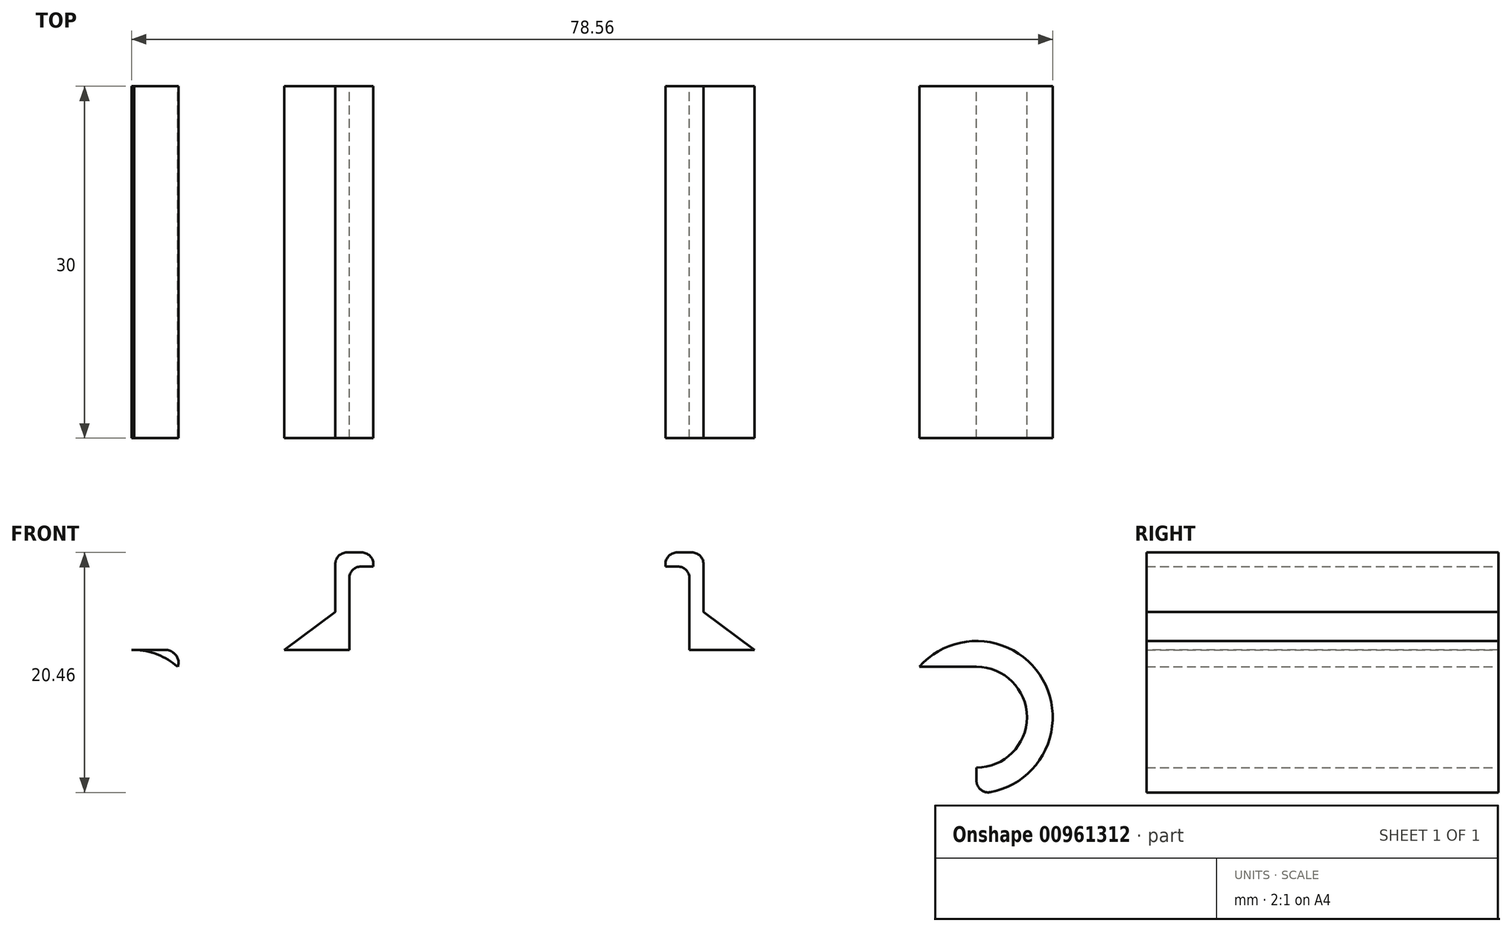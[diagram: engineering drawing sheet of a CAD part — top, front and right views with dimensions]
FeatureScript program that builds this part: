
annotation { "Feature Type Name" : "Feature", "Feature Type Description" : "" }
export const myFeature = defineFeature(function(context is Context, id is Id, definition is map)
    precondition{}
    {
        {
            var Q0;
            Q0=qCreatedBy(makeId("Front.planeOp"),FACE);
            var sketch = newSketch(context, id + "F0", { "sketchPlane" : qUnion([Q0])});
            skLineSegment(sketch, "E0", {"start": v(-37.32, 0) * mm, "end": v(43.18, 0) * mm});
            skCircle(sketch, "E1", {"center": v(-32.97, 0) * mm, "radius": 4.3 * mm});
            skCircle(sketch, "E2", {"center": v(38.98, 0) * mm, "radius": 4.3 * mm});
            skCircle(sketch, "E3", {"center": v(-32.97, 0) * mm, "radius": 5.75 * mm});
            skCircle(sketch, "E4", {"center": v(38.98, 0) * mm, "radius": 5.75 * mm});
            skLineSegment(sketch, "E5", {"start": v(-33.08, 5.75) * mm, "end": v(38.98, 5.75) * mm});
            skLineSegment(sketch, "E6.bottom", {"start": v(-14.5, 5.75) * mm, "end": v(-15.7, 5.75) * mm});
            skLineSegment(sketch, "E6.top", {"start": v(-14.5, 14.05) * mm, "end": v(-15.7, 14.05) * mm});
            skLineSegment(sketch, "E6.left", {"start": v(-14.5, 5.75) * mm, "end": v(-14.5, 14.05) * mm});
            skLineSegment(sketch, "E6.right", {"start": v(-15.7, 5.75) * mm, "end": v(-15.7, 14.05) * mm});
            skLineSegment(sketch, "E7.MirrorCS", {"start": v(14.5, 5.75) * mm, "end": v(14.5, 14.05) * mm});
            skLineSegment(sketch, "E8.MirrorCS", {"start": v(15.7, 5.75) * mm, "end": v(15.7, 14.05) * mm});
            skLineSegment(sketch, "E9.MirrorCS", {"start": v(14.5, 14.05) * mm, "end": v(15.7, 14.05) * mm});
            skLineSegment(sketch, "E10", {"start": v(-14.5, 9.9) * mm, "end": v(14.5, 9.9) * mm, "construction": true});
            skLineSegment(sketch, "E11.bottom", {"start": v(-14.5, 14.05) * mm, "end": v(-12.45, 14.05) * mm});
            skLineSegment(sketch, "E11.top", {"start": v(-14.5, 12.85) * mm, "end": v(-12.45, 12.85) * mm});
            skLineSegment(sketch, "E11.left", {"start": v(-14.5, 14.05) * mm, "end": v(-14.5, 12.85) * mm});
            skLineSegment(sketch, "E11.right", {"start": v(-12.45, 14.05) * mm, "end": v(-12.45, 12.85) * mm});
            skLineSegment(sketch, "E12", {"start": v(-15.7, 8.98) * mm, "end": v(-20.06, 5.75) * mm});
            skLineSegment(sketch, "E13.MirrorCS", {"start": v(14.5, 12.85) * mm, "end": v(12.45, 12.85) * mm});
            skLineSegment(sketch, "E14.MirrorCS", {"start": v(12.45, 14.05) * mm, "end": v(12.45, 12.85) * mm});
            skLineSegment(sketch, "E15.MirrorCS", {"start": v(14.5, 14.05) * mm, "end": v(12.45, 14.05) * mm});
            skLineSegment(sketch, "E16.MirrorCS", {"start": v(15.7, 8.98) * mm, "end": v(20.06, 5.75) * mm});
            skLineSegment(sketch, "E17", {"start": v(-604.46, 5.74) * mm, "end": v(-604.46, 4.54) * mm});
            skLineSegment(sketch, "E18", {"start": v(-33.1, 4.3) * mm, "end": v(38.98, 4.3) * mm});
            skCircle(sketch, "E19", {"center": v(-32.97, 0) * mm, "radius": 6.5 * mm});
            skCircle(sketch, "E20", {"center": v(38.98, 0) * mm, "radius": 6.5 * mm});
            skLineSegment(sketch, "E21", {"start": v(-33.1, 4.3) * mm, "end": v(-33.1, -12) * mm});
            skLineSegment(sketch, "E22", {"start": v(38.98, 4.3) * mm, "end": v(38.98, -15.81) * mm});
            skSolve(sketch);
        }
        {
            var Q0;
            {var subQ4=sQuery(id+"F0.wireOp",EDGE,"E4");var subQ6=makeQuery(id+"F0.imprint","INTERSECT",VERTEX,{"derivedFrom":[subQ4,sQuery(id+"F0.wireOp",EDGE,"E5")]});Q0=makeQuery(id+"F0.imprint","IMPRINT",FACE,{"disambiguationData":[TD([[makeQuery(id+"F0.imprint","IMPRINT",EDGE,{"disambiguationData":[TD([[subQ6,-1.0]])],"derivedFrom":subQ4}),1.0]])]});}
            var Q1;
            {var subQ4=sQuery(id+"F0.wireOp",EDGE,"E6.bottom");Q1=makeQuery(id+"F0.imprint","IMPRINT",FACE,{"disambiguationData":[TD([[makeQuery(id+"F0.imprint","IMPRINT",EDGE,{"derivedFrom":subQ4}),1.0]])]});}
            var Q2;
            {var subQ0=sQuery(id+"F0.wireOp",EDGE,"E5");var subQ1=sQuery(id+"F0.wireOp",EDGE,"E3");var subQ9=makeQuery(id+"F0.imprint","INTERSECT",VERTEX,{"disambiguationData":[OD(1.0)],"derivedFrom":[subQ1,subQ0]});Q2=makeQuery(id+"F0.imprint","IMPRINT",FACE,{"disambiguationData":[TD([[makeQuery(id+"F0.imprint","IMPRINT",EDGE,{"disambiguationData":[TD([[subQ9,1.0]])],"derivedFrom":subQ1}),1.0]])]});}
            var Q3;
            {var subQ3=sQuery(id+"F0.wireOp",EDGE,"E12");Q3=makeQuery(id+"F0.imprint","IMPRINT",FACE,{"disambiguationData":[TD([[makeQuery(id+"F0.imprint","IMPRINT",EDGE,{"derivedFrom":subQ3}),1.0]])]});}
            var Q4;
            {var subQ1=sQuery(id+"F0.wireOp",EDGE,"E6.bottom");Q4=makeQuery(id+"F0.imprint","IMPRINT",FACE,{"disambiguationData":[TD([[makeQuery(id+"F0.imprint","IMPRINT",EDGE,{"derivedFrom":subQ1}),-1.0]])]});}
            var Q5;
            {var subQ2=sQuery(id+"F0.wireOp",EDGE,"E13.MirrorCS");Q5=makeQuery(id+"F0.imprint","IMPRINT",FACE,{"disambiguationData":[TD([[makeQuery(id+"F0.imprint","IMPRINT",EDGE,{"derivedFrom":subQ2}),-1.0]])]});}
            var Q6;
            Q6=makeQuery(id+"F0.imprint","IMPRINT",FACE,{"disambiguationData":[TD([[makeQuery(id+"F0.imprint","IMPRINT",EDGE,{"derivedFrom":sQuery(id+"F0.wireOp",EDGE,"E11.bottom")}),-1.0]])]});
            var Q7;
            {var subQ0=sQuery(id+"F0.wireOp",EDGE,"E9.MirrorCS");Q7=makeQuery(id+"F0.imprint","IMPRINT",FACE,{"disambiguationData":[TD([[makeQuery(id+"F0.imprint","IMPRINT",EDGE,{"derivedFrom":subQ0}),-1.0]])]});}
            var Q8;
            {var subQ0=sQuery(id+"F0.wireOp",EDGE,"E16.MirrorCS");var subQ1=sQuery(id+"F0.wireOp",EDGE,"E5");var subQ2=makeQuery(id+"F0.imprint","INTERSECT",VERTEX,{"derivedFrom":[subQ1,subQ0]});Q8=makeQuery(id+"F0.imprint","IMPRINT",FACE,{"disambiguationData":[TD([[makeQuery(id+"F0.imprint","IMPRINT",EDGE,{"disambiguationData":[TD([[subQ2,1.0]])],"derivedFrom":subQ1}),1.0]])]});}
            var Q9;
            {var subQ3=sQuery(id+"F0.wireOp",EDGE,"E5");var subQ5=sQuery(id+"F0.wireOp",EDGE,"E3");var subQ8=makeQuery(id+"F0.imprint","INTERSECT",VERTEX,{"disambiguationData":[OD(0.0)],"derivedFrom":[subQ5,subQ3]});Q9=makeQuery(id+"F0.imprint","IMPRINT",FACE,{"disambiguationData":[TD([[makeQuery(id+"F0.imprint","IMPRINT",EDGE,{"disambiguationData":[TD([[subQ8,1.0]])],"derivedFrom":subQ5}),-1.0]])]});}
            var Q10;
            {var subQ0=sQuery(id+"F0.wireOp",EDGE,"E18");var subQ1=sQuery(id+"F0.wireOp",EDGE,"E3");var subQ2=makeQuery(id+"F0.imprint","INTERSECT",VERTEX,{"derivedFrom":[subQ1,subQ0]});Q10=makeQuery(id+"F0.imprint","IMPRINT",FACE,{"disambiguationData":[TD([[makeQuery(id+"F0.imprint","IMPRINT",EDGE,{"disambiguationData":[TD([[subQ2,-1.0]])],"derivedFrom":subQ1}),-1.0]])]});}
            var Q11;
            {var subQ0=sQuery(id+"F0.wireOp",EDGE,"E5");var subQ1=sQuery(id+"F0.wireOp",EDGE,"E4");var subQ2=makeQuery(id+"F0.imprint","INTERSECT",VERTEX,{"derivedFrom":[subQ1,subQ0]});Q11=makeQuery(id+"F0.imprint","IMPRINT",FACE,{"disambiguationData":[TD([[makeQuery(id+"F0.imprint","IMPRINT",EDGE,{"disambiguationData":[TD([[subQ2,1.0]])],"derivedFrom":subQ1}),-1.0]])]});}
            var Q12;
            {var subQ0=sQuery(id+"F0.wireOp",EDGE,"E5");var subQ1=sQuery(id+"F0.wireOp",EDGE,"E4");var subQ2=makeQuery(id+"F0.imprint","INTERSECT",VERTEX,{"derivedFrom":[subQ1,subQ0]});Q12=makeQuery(id+"F0.imprint","IMPRINT",FACE,{"disambiguationData":[TD([[makeQuery(id+"F0.imprint","IMPRINT",EDGE,{"disambiguationData":[TD([[subQ2,-1.0]])],"derivedFrom":subQ1}),-1.0]])]});}
            extrude(context, id + "F1", {"entities" : qUnion([Q0, Q1, Q2, Q3, Q4, Q5, Q6, Q7, Q8, Q9, Q10, Q11, Q12]), "depth" : 30 * mm, "offsetDistance" : 25 * mm});
        }
        {
            var Q0;
            Q0=makeQuery(id+"F1.opExtrude","SWEPT_EDGE",EDGE,{"disambiguationData":[OSD([sQuery(id+"F0.wireOp",EDGE,"E8.MirrorCS"),sQuery(id+"F0.wireOp",EDGE,"E9.MirrorCS")])]});
            var Q1;
            Q1=makeQuery(id+"F1.opExtrude","SWEPT_EDGE",EDGE,{"disambiguationData":[OSD([sQuery(id+"F0.wireOp",EDGE,"E6.top"),sQuery(id+"F0.wireOp",EDGE,"E6.right")])]});
            var Q2;
            Q2=makeQuery(id+"F1.opExtrude","SWEPT_EDGE",EDGE,{"disambiguationData":[OSD([sQuery(id+"F0.wireOp",EDGE,"E6.left"),sQuery(id+"F0.wireOp",EDGE,"E11.top"),sQuery(id+"F0.wireOp",EDGE,"E11.left")])]});
            var Q3;
            Q3=makeQuery(id+"F1.opExtrude","SWEPT_EDGE",EDGE,{"disambiguationData":[OSD([sQuery(id+"F0.wireOp",EDGE,"E7.MirrorCS"),sQuery(id+"F0.wireOp",EDGE,"E13.MirrorCS")])]});
            var Q4;
            Q4=makeQuery(id+"F1.opExtrude","SWEPT_EDGE",EDGE,{"disambiguationData":[OSD([sQuery(id+"F0.wireOp",EDGE,"E14.MirrorCS"),sQuery(id+"F0.wireOp",EDGE,"E15.MirrorCS")])]});
            var Q5;
            Q5=makeQuery(id+"F1.opExtrude","SWEPT_EDGE",EDGE,{"disambiguationData":[OSD([sQuery(id+"F0.wireOp",EDGE,"E11.bottom"),sQuery(id+"F0.wireOp",EDGE,"E11.right")])]});
            var Q6;
            Q6=makeQuery(id+"F1.opExtrude","SWEPT_EDGE",EDGE,{"disambiguationData":[OSD([sQuery(id+"F0.wireOp",EDGE,"E20"),sQuery(id+"F0.wireOp",EDGE,"E22")])]});
            var Q7;
            Q7=makeQuery(id+"F1.opExtrude","SWEPT_EDGE",EDGE,{"disambiguationData":[OSD([sQuery(id+"F0.wireOp",EDGE,"E19"),sQuery(id+"F0.wireOp",EDGE,"E21")])]});
            fillet(context, id + "F2", {"entities" : qUnion([Q0, Q1, Q2, Q3, Q4, Q5, Q6, Q7]), "radius" : 1 * mm, "tangentPropagation" : true, "allowEdgeOverflow" : false});
        }
    });
